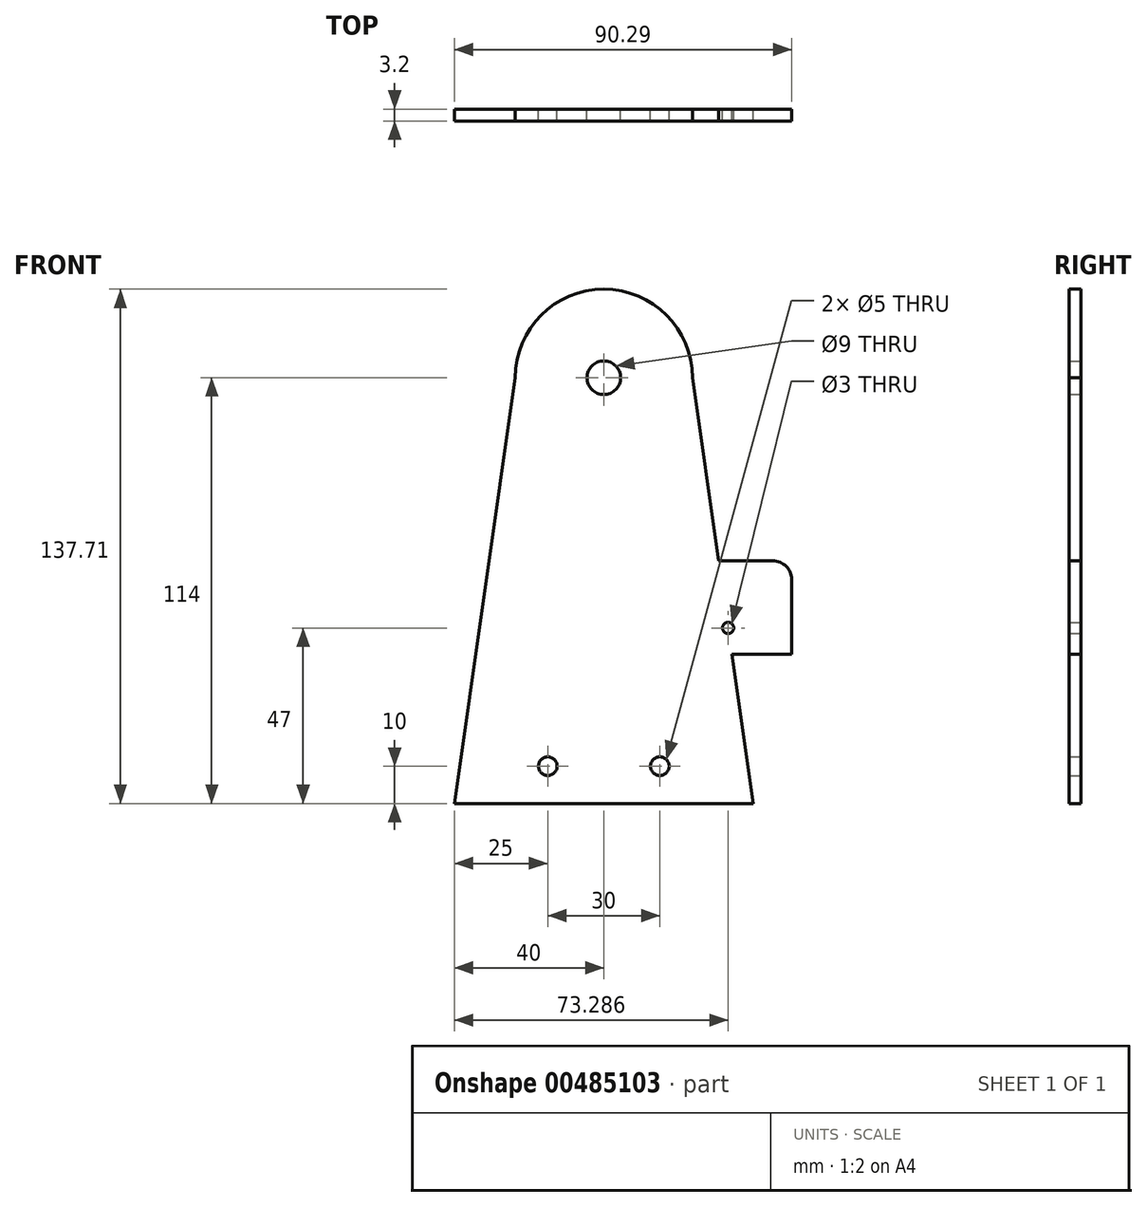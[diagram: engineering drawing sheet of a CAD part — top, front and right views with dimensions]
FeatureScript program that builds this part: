
annotation { "Feature Type Name" : "Feature", "Feature Type Description" : "" }
export const myFeature = defineFeature(function(context is Context, id is Id, definition is map)
    precondition{}
    {
        {
            var Q0;
            Q0=qCreatedBy(makeId("Front.planeOp"),FACE);
            var sketch = newSketch(context, id + "F0", { "sketchPlane" : qUnion([Q0])});
            skLineSegment(sketch, "E0.bottom", {"start": v(-40, 70) * mm, "end": v(40, 70) * mm, "construction": true});
            skLineSegment(sketch, "E0.top", {"start": v(-40, -70) * mm, "end": v(40, -70) * mm, "construction": true});
            skLineSegment(sketch, "E0.left", {"start": v(-40, 70) * mm, "end": v(-40, -70) * mm, "construction": true});
            skLineSegment(sketch, "E0.right", {"start": v(40, 70) * mm, "end": v(40, -70) * mm, "construction": true});
            skPoint(sketch, "E0.middle", {"position": v(0, 0) * mm});
            skLineSegment(sketch, "E1", {"start": v(-40, 70) * mm, "end": v(-20, 70) * mm});
            skLineSegment(sketch, "E2", {"start": v(40, 70) * mm, "end": v(20, 70) * mm});
            skLineSegment(sketch, "E3", {"start": v(-40, -70) * mm, "end": v(-20, 70) * mm, "construction": true});
            skLineSegment(sketch, "E4", {"start": v(0, 70) * mm, "end": v(0, 44) * mm, "construction": true});
            skPoint(sketch, "E4.endSnap0", {"position": v(0, 70) * mm});
            skLineSegment(sketch, "E5", {"start": v(0, 44) * mm, "end": v(23.71, 44) * mm, "construction": true});
            skLineSegment(sketch, "E6", {"start": v(0, 44) * mm, "end": v(-23.71, 44) * mm, "construction": true});
            skArc(sketch, "E7", {"start": v(23.71, 44) * mm, "mid": v(0, 67.71) * mm, "end": v(-23.71, 44) * mm, "construction": true});
            skLineSegment(sketch, "E8", {"start": v(-40, -70) * mm, "end": v(-23.71, 44) * mm});
            skLineSegment(sketch, "E9", {"start": v(-40, -70) * mm, "end": v(40, -70) * mm});
            skArc(sketch, "E10", {"start": v(23.71, 44) * mm, "mid": v(0, 67.71) * mm, "end": v(-23.71, 44) * mm});
            skCircle(sketch, "E11", {"center": v(0, 44) * mm, "radius": 4.5 * mm});
            skLineSegment(sketch, "E12", {"start": v(-38.57, -60) * mm, "end": v(38.57, -60) * mm, "construction": true});
            skLineSegment(sketch, "E13", {"start": v(-15, -60) * mm, "end": v(-15, -70) * mm, "construction": true});
            skLineSegment(sketch, "E14", {"start": v(15, -70) * mm, "end": v(15, -60) * mm, "construction": true});
            skCircle(sketch, "E15", {"center": v(-15, -60) * mm, "radius": 2.5 * mm});
            skCircle(sketch, "E16", {"center": v(15, -60) * mm, "radius": 2.5 * mm});
            skLineSegment(sketch, "E17", {"start": v(20, 70) * mm, "end": v(40, -70) * mm, "construction": true});
            skLineSegment(sketch, "E18", {"start": v(-30.71, -5) * mm, "end": v(30.71, -5) * mm, "construction": true});
            skLineSegment(sketch, "E19", {"start": v(-34.29, -30) * mm, "end": v(34.29, -30) * mm, "construction": true});
            skLineSegment(sketch, "E20", {"start": v(34.29, -30) * mm, "end": v(50.29, -30) * mm, "construction": true});
            skLineSegment(sketch, "E21", {"start": v(40, -70) * mm, "end": v(34.29, -30) * mm});
            skLineSegment(sketch, "E22", {"start": v(50.29, -30) * mm, "end": v(34.29, -30) * mm});
            skLineSegment(sketch, "E23", {"start": v(30.71, -5) * mm, "end": v(23.71, 44) * mm});
            skLineSegment(sketch, "E24", {"start": v(30.71, -5) * mm, "end": v(50.29, -5) * mm, "construction": true});
            skLineSegment(sketch, "E25", {"start": v(50.29, -5) * mm, "end": v(50.29, -30) * mm, "construction": true});
            skLineSegment(sketch, "E26", {"start": v(34.29, -30) * mm, "end": v(34.29, -5) * mm, "construction": true});
            skLineSegment(sketch, "E27", {"start": v(50.29, -30) * mm, "end": v(50.29, -5) * mm});
            skLineSegment(sketch, "E28", {"start": v(50.29, -5) * mm, "end": v(30.71, -5) * mm});
            skLineSegment(sketch, "E29", {"start": v(33.29, -5) * mm, "end": v(33.29, -30) * mm, "construction": true});
            skLineSegment(sketch, "E30", {"start": v(34.29, -12) * mm, "end": v(50.29, -12) * mm, "construction": true});
            skLineSegment(sketch, "E31", {"start": v(50.29, -23) * mm, "end": v(34.29, -23) * mm, "construction": true});
            skCircle(sketch, "E32", {"center": v(33.29, -12) * mm, "radius": 1.5 * mm, "construction": true});
            skCircle(sketch, "E33", {"center": v(33.29, -23) * mm, "radius": 1.5 * mm});
            skSolve(sketch);
        }
        {
            var Q0;
            Q0=makeQuery(id+"F0.imprint","IMPRINT",FACE,{"disambiguationData":[TD([[makeQuery(id+"F0.imprint","IMPRINT",EDGE,{"derivedFrom":sQuery(id+"F0.wireOp",EDGE,"E8")}),-1.0]])]});
            extrude(context, id + "F1", {"entities" : qUnion([Q0]), "depth" : 3.2 * mm});
        }
        {
            var Q0;
            Q0=makeQuery(id+"F1.opExtrude","SWEPT_EDGE",EDGE,{"disambiguationData":[OSD([sQuery(id+"F0.wireOp",EDGE,"E27"),sQuery(id+"F0.wireOp",EDGE,"E28")])]});
            fillet(context, id + "F2", {"entities" : qUnion([Q0]), "radius" : 5 * mm, "tangentPropagation" : true, "allowEdgeOverflow" : false});
        }
    });
